# Revit family: Rheem AP Vitreous Enamel HWC
name_source: partatom
category: Plumbing Fixtures
units: mm (PartAtom-declared; Revit-internal decimal feet)

## family parameters
Always vertical = Yes
Cut with Voids When Loaded = No
Enable Cutting in Views = No
Maintain Annotation Orientation = No
OmniClass Number = 23.45.00.00
OmniClass Title = Sanitary, Laundry, and Cleaning Equipment
Part Type = Normal
Room Calculation Point = No
Round Connector Dimension = Use Diameter
Shared = No
Work Plane-Based = No

## types (27) — shared parameters
C - Height = 135 mm  [stored 0.442913 ft]
Connection D = Yes
D - Height = 80 mm  [stored 0.262467 ft]
H - Angle = 36.00°
Manufacturer = Rheem
Material = <By Category>
Top Connection Size = 75 mm
URL = https://rheem.co.nz
zero-valued in all types: Boost Capacity (Twin Element), Default Elevation

## per-type parameters (varying)
| type | A - Height | Approx. Storage Capacity | B - Width | Connection - D | Connection Length | Element Rating (@230V) | Model | Top Connection Placement |
| APVE 90L 490 x 920H Triple Inlet 2kW | 920 mm  [stored 3.01837 ft] | 90 m³ | 490 mm  [stored 1.60761 ft] | 255 mm  [stored 0.836614 ft] | 255 mm  [stored 0.836614 ft] | 2000 W | 14809013AP | 123 mm |
| APVE 90L 490 x 920H Triple Inlet 3kW | 920 mm  [stored 3.01837 ft] | 90 m³ | 490 mm  [stored 1.60761 ft] | 255 mm  [stored 0.836614 ft] | 255 mm  [stored 0.836614 ft] | 3000 W | 14809015AP | 123 mm |
| APVE 135L 490 x 1320H Triple Inlet 2kW | 1320 mm | 135 m³ | 490 mm  [stored 1.60761 ft] | 255 mm  [stored 0.836614 ft] | 255 mm  [stored 0.836614 ft] | 2000 W | 14813513AP | 123 mm |
| APVE 135L 490 x 1320H Triple Inlet 3kW | 1320 mm | 135 m³ | 490 mm  [stored 1.60761 ft] | 255 mm  [stored 0.836614 ft] | 255 mm  [stored 0.836614 ft] | 3000 W | 14813515AP | 123 mm |
| APVE 180L 490 x 1715H Triple Inlet 2kW | 1715 mm  [stored 5.62664 ft] | 180 m³ | 490 mm  [stored 1.60761 ft] | 255 mm  [stored 0.836614 ft] | 255 mm  [stored 0.836614 ft] | 2000 W | 14818013AP | 123 mm |
| APVE 180L 490 x 1715H Triple Inlet 3kW | 1715 mm  [stored 5.62664 ft] | 180 m³ | 490 mm  [stored 1.60761 ft] | 255 mm  [stored 0.836614 ft] | 255 mm  [stored 0.836614 ft] | 3000 W | 14818015AP | 123 mm |
| APVE 90L 510 x 780H Triple Inlet 2kW | 780 mm  [stored 2.55906 ft] | 90 m³ | 510 mm  [stored 1.67323 ft] | 265 mm  [stored 0.869423 ft] | 265 mm  [stored 0.869423 ft] | 2000 W | 14T09013AP | 128 mm |
| APVE 110L 510 x 945H Triple Inlet 2kW | 945 mm  [stored 3.10039 ft] | 110 m³ | 510 mm  [stored 1.67323 ft] | 265 mm  [stored 0.869423 ft] | 265 mm  [stored 0.869423 ft] | 2000 W | 14T11013AP | 128 mm |
| APVE 135L 510 x 1140H Triple Inlet 2kW | 1140 mm  [stored 3.74016 ft] | 135 m³ | 510 mm  [stored 1.67323 ft] | 265 mm  [stored 0.869423 ft] | 265 mm  [stored 0.869423 ft] | 2000 W | 16T13513AP | 128 mm |
| APVE 180L 510 x 1510H Triple Inlet 2kW | 1510 mm  [stored 4.95407 ft] | 180 m³ | 510 mm  [stored 1.67323 ft] | 265 mm  [stored 0.869423 ft] | 265 mm  [stored 0.869423 ft] | 2000 W | 16T18013AP | 128 mm |
| APVE 180L 510 x 1510H Triple Inlet 3kW | 1510 mm  [stored 4.95407 ft] | 180 m³ | 510 mm  [stored 1.67323 ft] | 265 mm  [stored 0.869423 ft] | 265 mm  [stored 0.869423 ft] | 3000 W | 16T18015AP | 128 mm |
| APVE 135L 540 x 1030H Triple Inlet 2kW | 1030 mm  [stored 3.37927 ft] | 135 m³ | 540 mm  [stored 1.77165 ft] | 280 mm  [stored 0.918635 ft] | 280 mm  [stored 0.918635 ft] | 2000 W | 54T13513AP | 135 mm  [stored 0.442913 ft] |
| APVE 180L 540 x 1350H Triple Inlet 2kW | 1350 mm  [stored 4.42913 ft] | 180 m³ | 540 mm  [stored 1.77165 ft] | 280 mm  [stored 0.918635 ft] | 280 mm  [stored 0.918635 ft] | 2000 W | 54T18013AP | 135 mm  [stored 0.442913 ft] |
| APVE 180L 540 x 1350H Triple Inlet 3kW | 1350 mm  [stored 4.42913 ft] | 180 m³ | 540 mm  [stored 1.77165 ft] | 280 mm  [stored 0.918635 ft] | 280 mm  [stored 0.918635 ft] | 3000 W | 54T18015AP | 135 mm  [stored 0.442913 ft] |
| APVE 135L 560 x 950H Triple Inlet 2kW | 950 mm  [stored 3.1168 ft] | 135 m³ | 560 mm  [stored 1.83727 ft] | 290 mm  [stored 0.951444 ft] | 290 mm  [stored 0.951444 ft] | 2000 W | 14T13513AP | 140 mm  [stored 0.459318 ft] |
| APVE 180L 560 x 1220H Triple Inlet 2kW | 1220 mm  [stored 4.00262 ft] | 180 m³ | 560 mm  [stored 1.83727 ft] | 290 mm  [stored 0.951444 ft] | 290 mm  [stored 0.951444 ft] | 2000 W | 14T18013AP | 140 mm  [stored 0.459318 ft] |
| APVE 180L 560 x 1220H Triple Inlet 3kW | 1220 mm  [stored 4.00262 ft] | 180 m³ | 560 mm  [stored 1.83727 ft] | 290 mm  [stored 0.951444 ft] | 290 mm  [stored 0.951444 ft] | 3000 W | 14T18015AP | 140 mm  [stored 0.459318 ft] |
| APVE 250L 560 x 1710H Triple Inlet 3kW | 1710 mm  [stored 5.61024 ft] | 250 m³ | 560 mm  [stored 1.83727 ft] | 290 mm  [stored 0.951444 ft] | 290 mm  [stored 0.951444 ft] | 3000 W | 14T25015AP | 140 mm  [stored 0.459318 ft] |
| APVE 135L 580 x 885H Triple Inlet 2kW | 885 mm | 135 m³ | 580 mm  [stored 1.90289 ft] | 300 mm  [stored 0.984252 ft] | 300 mm  [stored 0.984252 ft] | 2000 W | 15813513AP | 145 mm  [stored 0.475722 ft] |
| APVE 135L 580 x 885H Triple Inlet 3kW | 885 mm | 135 m³ | 580 mm  [stored 1.90289 ft] | 300 mm  [stored 0.984252 ft] | 300 mm  [stored 0.984252 ft] | 3000 W | 15813515AP | 145 mm  [stored 0.475722 ft] |
| APVE 180L 580 x 1140H Triple Inlet 2kW | 1140 mm  [stored 3.74016 ft] | 180 m³ | 580 mm  [stored 1.90289 ft] | 300 mm  [stored 0.984252 ft] | 300 mm  [stored 0.984252 ft] | 2000 W | 15818013AP | 145 mm  [stored 0.475722 ft] |
| APVE 180L 580 x 1140H Triple Inlet 3kW | 1140 mm  [stored 3.74016 ft] | 180 m³ | 580 mm  [stored 1.90289 ft] | 300 mm  [stored 0.984252 ft] | 300 mm  [stored 0.984252 ft] | 3000 W | 15818015AP | 145 mm  [stored 0.475722 ft] |
| APVE 250L 580 x 1540H Triple Inlet 3kW | 1540 mm  [stored 5.05249 ft] | 250 m³ | 580 mm  [stored 1.90289 ft] | 300 mm  [stored 0.984252 ft] | 300 mm  [stored 0.984252 ft] | 3000 W | 15825015AP | 145 mm  [stored 0.475722 ft] |
| APVE 135L 610 x 795H Triple Inlet 2kW | 795 mm  [stored 2.60827 ft] | 135 m³ | 610 mm  [stored 2.00131 ft] | 315 mm  [stored 1.03346 ft] | 315 mm  [stored 1.03346 ft] | 2000 W | 12T13513AP | 153 mm |
| APVE 180L 610 x 1015H Triple Inlet 2kW | 1015 mm  [stored 3.33005 ft] | 180 m³ | 610 mm  [stored 2.00131 ft] | 315 mm  [stored 1.03346 ft] | 315 mm  [stored 1.03346 ft] | 2000 W | 12T18013AP | 153 mm |
| APVE 180L 610 x 1015H Triple Inlet 3kW | 1015 mm  [stored 3.33005 ft] | 180 m³ | 610 mm  [stored 2.00131 ft] | 315 mm  [stored 1.03346 ft] | 315 mm  [stored 1.03346 ft] | 3000 W | 12T18015AP | 153 mm |
| APVE 250L 610 x 1410H Triple Inlet 3kW | 1410 mm  [stored 4.62598 ft] | 250 m³ | 610 mm  [stored 2.00131 ft] | 315 mm  [stored 1.03346 ft] | 315 mm  [stored 1.03346 ft] | 3000 W | 12T25015AP | 153 mm |

note: column(s) folded — value = type name in every type: Description

note: [stored X ft] marks values corroborated as IEEE doubles in the binary element streams (Revit-internal decimal feet)

## geometry (parser evidence)
native form markers: Sweep x3
no freeform markers — native parametric forms only
